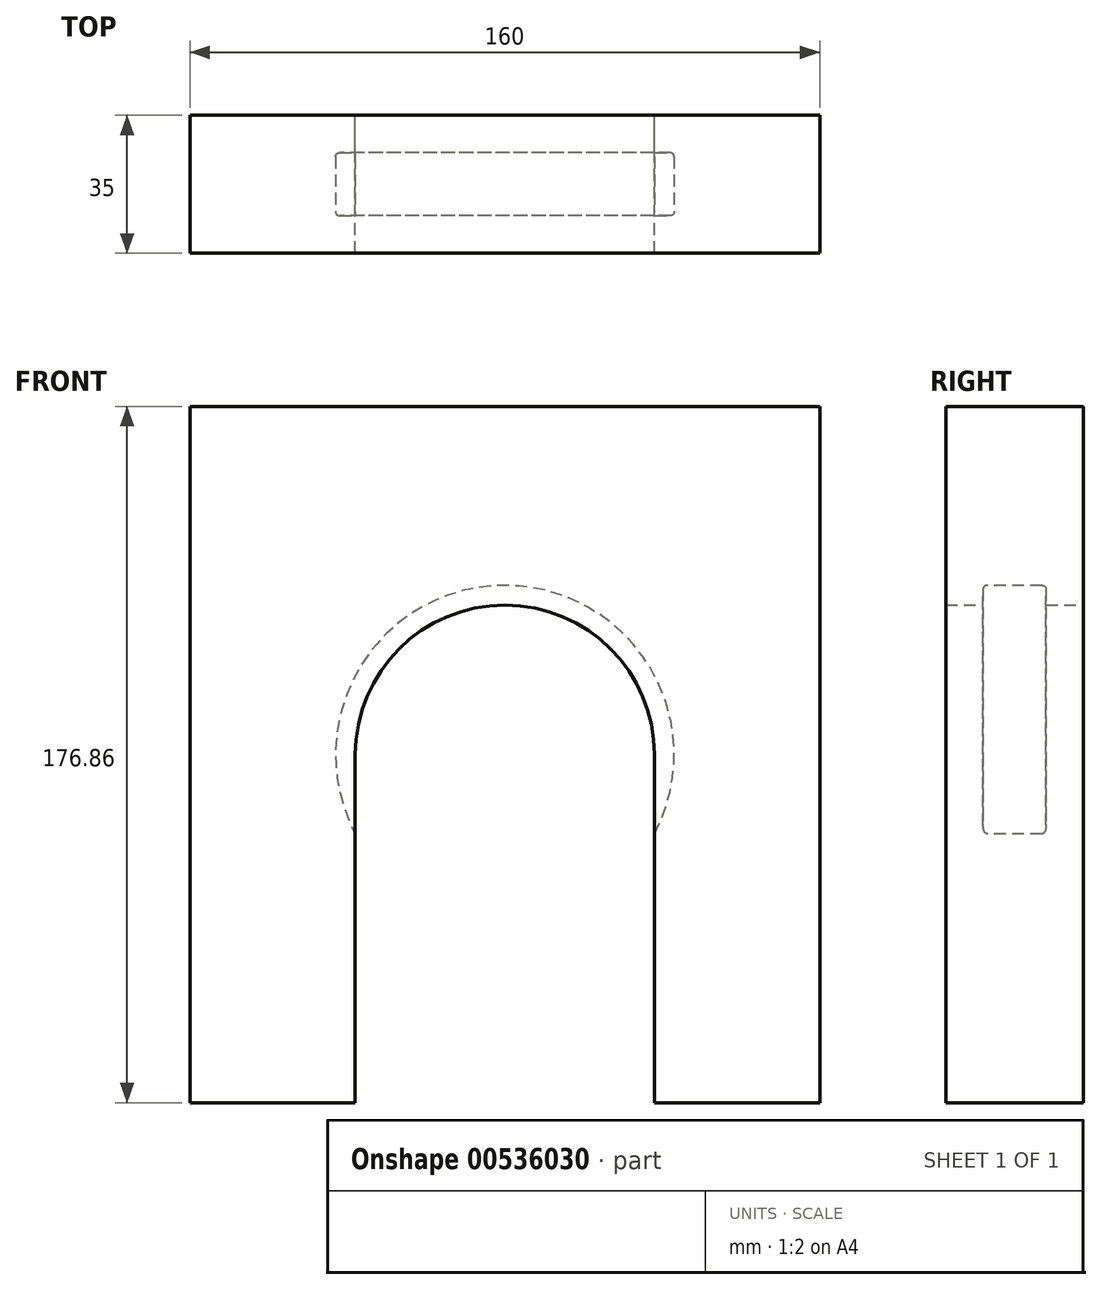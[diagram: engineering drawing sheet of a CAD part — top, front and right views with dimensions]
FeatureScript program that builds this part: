
annotation { "Feature Type Name" : "Feature", "Feature Type Description" : "" }
export const myFeature = defineFeature(function(context is Context, id is Id, definition is map)
    precondition{}
    {
        {
            var Q0;
            Q0=qCreatedBy(makeId("Front.planeOp"),FACE);
            var sketch = newSketch(context, id + "F0", { "sketchPlane" : qUnion([Q0])});
            skArc(sketch, "E0", {"start": v(38, 0) * mm, "mid": v(0, 38) * mm, "end": v(-38, 0) * mm});
            skLineSegment(sketch, "E1.bottom", {"start": v(-80, -88.43) * mm, "end": v(-38, -88.43) * mm});
            skLineSegment(sketch, "E1.top", {"start": v(-80, 88.43) * mm, "end": v(80, 88.43) * mm});
            skLineSegment(sketch, "E1.left", {"start": v(-80, -88.43) * mm, "end": v(-80, 88.43) * mm});
            skLineSegment(sketch, "E1.right", {"start": v(80, -88.43) * mm, "end": v(80, 88.43) * mm});
            skLineSegment(sketch, "E2", {"start": v(-38, 0) * mm, "end": v(-38, -88.43) * mm});
            skLineSegment(sketch, "E3", {"start": v(38, 0) * mm, "end": v(38, -88.43) * mm});
            skLineSegment(sketch, "E4.trimOffspring", {"start": v(38, -88.43) * mm, "end": v(80, -88.43) * mm});
            skSolve(sketch);
        }
        {
            var Q0;
            Q0 = qSketchRegion(id + "F0", true);
            extrude(context, id + "F1", {"entities" : qUnion([Q0]), "endBound" : BoundingType.SYMMETRIC, "depth" : 35 * mm, "offsetDistance" : 25 * mm});
        }
        {
            var Q0;
            Q0=qCreatedBy(makeId("Right.planeOp"),FACE);
            var sketch = newSketch(context, id + "F2", { "sketchPlane" : qUnion([Q0])});
            skLineSegment(sketch, "E5.0", {"start": v(-8, 32.88) * mm, "end": v(-8, 43) * mm});
            skLineSegment(sketch, "E6", {"start": v(-8, 43) * mm, "end": v(0, 43) * mm});
            skPoint(sketch, "E7.trimOffspring.end.orphan", {"position": v(0, 105) * mm});
            skLineSegment(sketch, "E8.MirrorCS", {"start": v(8, 43) * mm, "end": v(0, 43) * mm});
            skLineSegment(sketch, "E9.MirrorCS", {"start": v(8, 32.88) * mm, "end": v(8, 43) * mm});
            skLineSegment(sketch, "E10", {"start": v(-8, 32.88) * mm, "end": v(8, 32.88) * mm});
            skSolve(sketch);
        }
        {
            var Q0;
            Q0 = qSketchRegion(id + "F2", true);
            var Q1;
            Q1=makeQuery(id+"F1.opExtrude","SWEPT_FACE",FACE,{"disambiguationData":[OSD([sQuery(id+"F0.wireOp",EDGE,"E0")])]});
            revolve(context, id + "F3", {"operationType" : NewBodyOperationType.REMOVE, "entities" : qUnion([Q0]), "axis" : qUnion([Q1]), "revolveType" : RevolveType.FULL, "oppositeDirection" : true});
        }
        {
            var Q0;
            Q0=makeQuery(id+"F3.boolean.opBoolean","COPY",EDGE,{"derivedFrom":makeQuery(id+"F3.opRevolve","SWEPT_EDGE",EDGE,{"disambiguationData":[OSD([sQuery(id+"F2.wireOp",EDGE,"E8.MirrorCS"),sQuery(id+"F2.wireOp",EDGE,"E9.MirrorCS")])]})});
            fillet(context, id + "F4", {"entities" : qUnion([Q0]), "radius" : 1 * mm, "tangentPropagation" : true, "allowEdgeOverflow" : false});
        }
        {
            var Q0;
            Q0=makeQuery(id+"F3.boolean.opBoolean","COPY",EDGE,{"derivedFrom":makeQuery(id+"F3.opRevolve","SWEPT_EDGE",EDGE,{"disambiguationData":[OSD([sQuery(id+"F2.wireOp",EDGE,"E5.0"),sQuery(id+"F2.wireOp",EDGE,"E6")])]})});
            fillet(context, id + "F5", {"entities" : qUnion([Q0]), "radius" : 1 * mm, "tangentPropagation" : true, "allowEdgeOverflow" : false});
        }
    });
